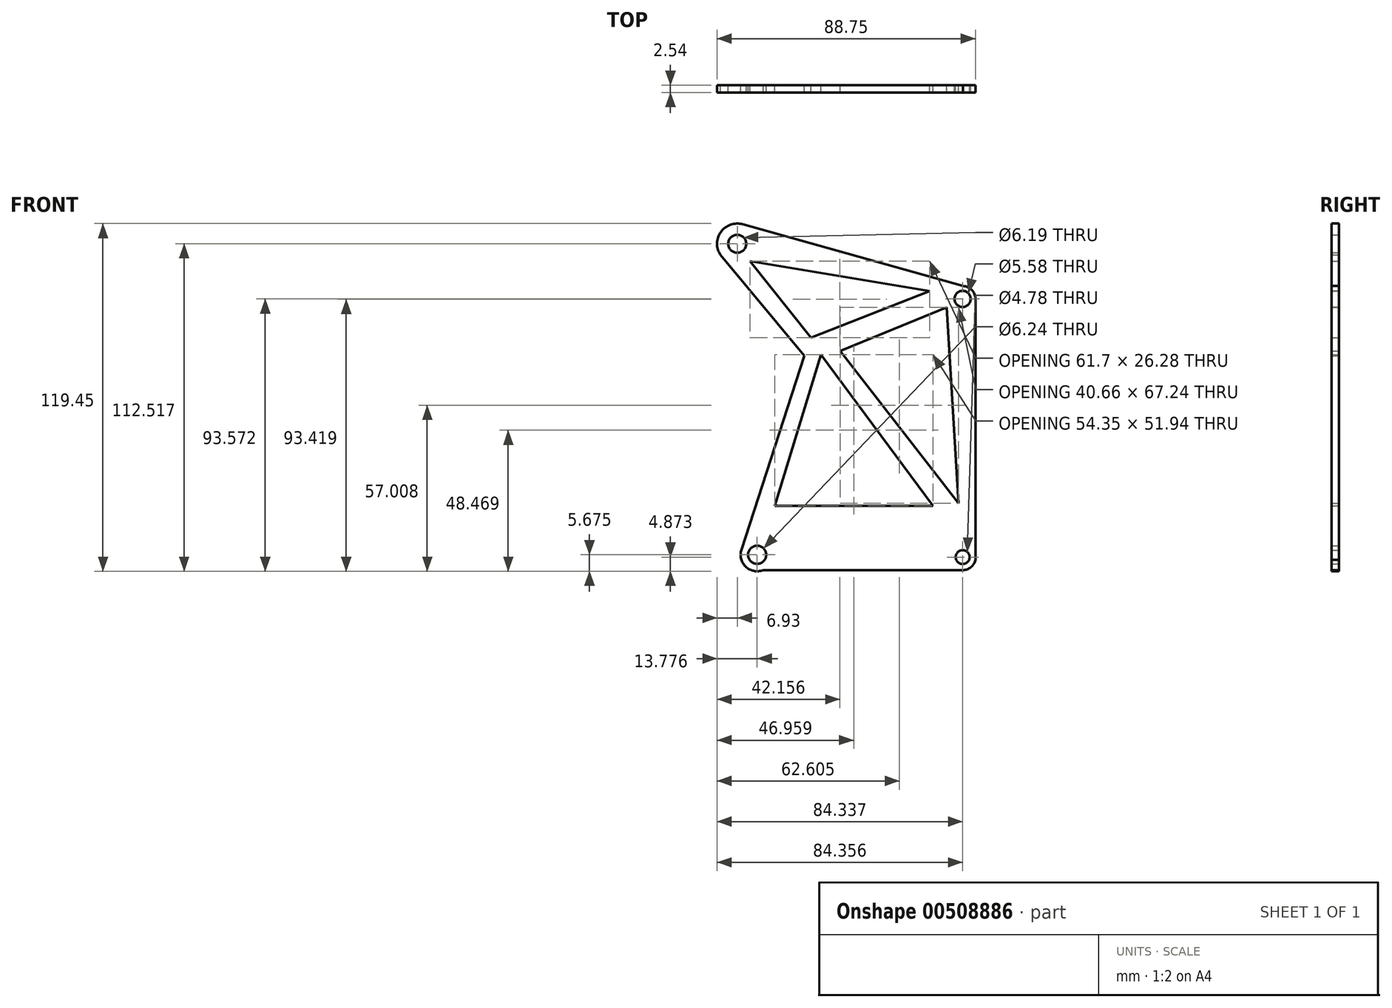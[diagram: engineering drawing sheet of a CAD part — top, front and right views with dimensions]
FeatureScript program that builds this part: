
annotation { "Feature Type Name" : "Feature", "Feature Type Description" : "" }
export const myFeature = defineFeature(function(context is Context, id is Id, definition is map)
    precondition{}
    {
        {
            var Q0;
            Q0=qCreatedBy(makeId("Front.planeOp"),FACE);
            var sketch = newSketch(context, id + "F0", { "sketchPlane" : qUnion([Q0])});
            skLineSegment(sketch, "E0", {"start": v(-34.94, -55.63) * mm, "end": v(33.59, -55.63) * mm});
            skArc(sketch, "E1", {"start": v(33.59, -55.63) * mm, "mid": v(36.4, -54.64) * mm, "end": v(37.98, -52.1) * mm});
            skLineSegment(sketch, "E2", {"start": v(37.98, -52.1) * mm, "end": v(37.98, 37.56) * mm});
            skArc(sketch, "E3", {"start": v(37.98, 37.56) * mm, "mid": v(36.74, 40.63) * mm, "end": v(33.72, 41.97) * mm});
            skLineSegment(sketch, "E4", {"start": v(33.72, 41.97) * mm, "end": v(-41.97, 63.18) * mm});
            skArc(sketch, "E5", {"start": v(-41.97, 63.18) * mm, "mid": v(-49.43, 60.6) * mm, "end": v(-49.65, 52.72) * mm});
            skLineSegment(sketch, "E6", {"start": v(-49.65, 52.72) * mm, "end": v(-20.83, 17.97) * mm});
            skLineSegment(sketch, "E7", {"start": v(-20.83, 17.97) * mm, "end": v(-42.4, -48.58) * mm});
            skArc(sketch, "E8", {"start": v(-42.4, -48.58) * mm, "mid": v(-40.9, -54.46) * mm, "end": v(-34.94, -55.63) * mm});
            skCircle(sketch, "E9", {"center": v(-43.84, 56.5) * mm, "radius": 3.1 * mm});
            skCircle(sketch, "E10", {"center": v(33.57, 37.56) * mm, "radius": 2.79 * mm});
            skCircle(sketch, "E11", {"center": v(33.59, -51.14) * mm, "radius": 2.4 * mm});
            skCircle(sketch, "E12", {"center": v(-37, -50.34) * mm, "radius": 3.12 * mm});
            skLineSegment(sketch, "E13", {"start": v(-30.99, -33.51) * mm, "end": v(23.37, -33.51) * mm});
            skLineSegment(sketch, "E14", {"start": v(23.37, -33.51) * mm, "end": v(-15.1, 18.43) * mm});
            skLineSegment(sketch, "E15", {"start": v(-15.1, 18.43) * mm, "end": v(-30.99, -33.51) * mm});
            skLineSegment(sketch, "E16", {"start": v(-18.45, 24.27) * mm, "end": v(-39.46, 50.55) * mm});
            skLineSegment(sketch, "E17", {"start": v(-39.46, 50.55) * mm, "end": v(22.23, 40.24) * mm});
            skLineSegment(sketch, "E18", {"start": v(22.23, 40.24) * mm, "end": v(-18.45, 24.27) * mm});
            skLineSegment(sketch, "E19", {"start": v(32.16, -32.62) * mm, "end": v(-8.5, 19.64) * mm});
            skLineSegment(sketch, "E20", {"start": v(-8.5, 19.64) * mm, "end": v(28.06, 34.62) * mm});
            skLineSegment(sketch, "E21", {"start": v(28.06, 34.62) * mm, "end": v(32.16, -32.62) * mm});
            skSolve(sketch);
        }
        {
            var Q0;
            Q0=makeQuery(id+"F0.imprint","IMPRINT",FACE,{"disambiguationData":[TD([[makeQuery(id+"F0.imprint","IMPRINT",EDGE,{"derivedFrom":sQuery(id+"F0.wireOp",EDGE,"E0")}),1.0]])]});
            extrude(context, id + "F1", {"entities" : qUnion([Q0]), "depth" : 2.54 * mm});
        }
    });
